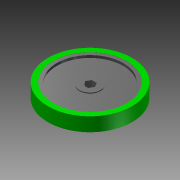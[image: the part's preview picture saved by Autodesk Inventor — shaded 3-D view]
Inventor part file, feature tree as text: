
AUTODESK INVENTOR PART (.ipt)
format: ipt  version: 2012 (Build 160160000, 160)  size: 125,952 bytes
history: native  units: mm
features: extrude x5, sketch x1
ambient origin geometry x8: Origin, YZ Plane, XZ Plane, XY Plane, X Axis, Y Axis, Z Axis, Center Point
bodies: Solid1 (feature_tree)
feature tree (6):
  sketch  "Sketch1"  dims[d0=8.0mm d2=12.7mm d3=12.7mm d4=0.0mm d5=20.32mm d6=0.0mm d7=123.825mm d8=13.0mm d9=10.0mm d10=0.0mm d11=10.0mm d12=0.0mm d13=31.0mm d14=15.24mm d15=0.0mm]
  extrude  "Extrusion1"  Depth=12.7mm
  extrude  "Extrusion2"  Depth=12.7mm TaperAngle=0.0deg
  extrude  "Extrusion3"  Depth=20.32mm TaperAngle=0.0deg
  extrude  "Extrusion4"  Depth=123.825mm
  extrude  "Extrusion5"  Depth=13.0mm
